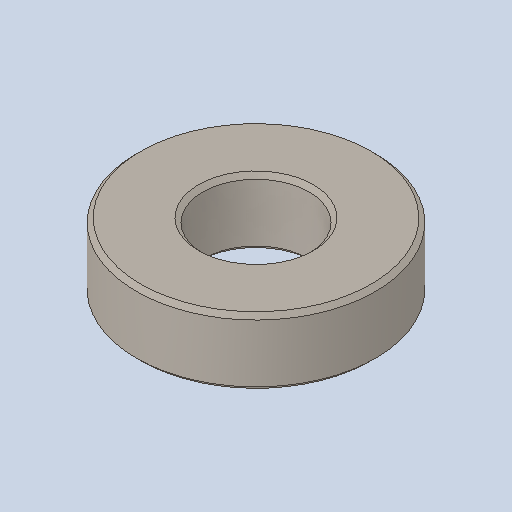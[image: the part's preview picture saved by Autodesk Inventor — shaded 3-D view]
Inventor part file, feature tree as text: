
AUTODESK INVENTOR PART (.ipt)
format: ipt  version: 2023.4 (Build 274418000, 418)  size: 102,400 bytes
history: native  units: in
note: dims shown in document units (in); Inventor stores cm internally (conversion verified against a paired STEP export)
features: chamfer x1
ambient origin geometry x8: Origin, YZ Plane, XZ Plane, XY Plane, X Axis, Y Axis, Z Axis, Center Point
bodies: Solid1 (feature_tree)
feature tree (1):
  chamfer  "Chamfer1"  [1 undecoded]
note: 1 required parameter value undecoded (feature->parameter linkage not recoverable at this tier; creation-order binding heuristic only, values carry confidence <= 0.55)
